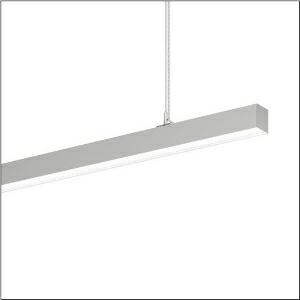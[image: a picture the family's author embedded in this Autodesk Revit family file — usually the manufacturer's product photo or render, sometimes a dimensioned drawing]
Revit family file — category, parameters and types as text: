
# Revit family: silica_r__21_51mx33tctds_657e
name_source: partatom
category: Lighting Fixtures
units: mm (PartAtom-declared; Revit-internal decimal feet)

## family parameters
Cut with Voids When Loaded = No
Host = Face
Light Source = No
Part Type = Normal
Room Calculation Point = No
Round Connector Dimension = Use Diameter
Shared = No

## types (1)
- --- (1 x LED, 14340 lm, 134.7 W, 6500K)
    Apparent Load = 135 VA
    CIE Flux Codes = 78 96 99 56 100
    Color Rendering = 80
    Color Temperature = 6500K
    Default Elevation = 1800 mm
    Description = Silica® 21, office luminaire, primary optical cover: prismatic diffuser, of PMMA, CAT 2 (L<= 3000cd/m²), light emission: direct/indirect distribution, primary light characteristic: symmetric, installation type: suspended mounting, LED, rated luminous flux: 14.340lm, luminous efficacy: 101lm/W, light colour: 8tw, colour temperature: 2700..6500K, control gear: DALI DT8, with terminal, 3+2-pole, max. 2.5mm², mains connection: 220..240V, AC, 50/60Hz, rated input power: 141.4W, luminaire housing, of aluminium, metallic grey (RAL 9006), length: 3.004mm, width: 53mm, height: 53mm, protection rating (complete): IP20, insulation class (complete): insulation class I (protective earthing), certification: CE, permissible operating ambient temperature: 0..+35°C, standard: EN 50419, packaging unit: 1 piece
    Height = 53 mm
    Lamp = 1 x LED
    Lamp Light Flux = 14340 lm
    Lamp Power = 134.7 W
    Lamp count = 1
    Length = 3004 mm
    Luminous efficacy = 106 lm/W
    Manufacturer = Siteco
    ModVariant = No
    Model = 51MX33TCTDS
    Mounting Place = Ceiling
    Mounting Type = Pendant
    Number of Poles = 1
    OnlyDefault = Yes
    Power Factor = 1
    Product Name = Silica® 21
    Product group = office luminaire | ceiling pendant
    ProductGroupID = 904
    Protection Class = Protection class I
    Protection Degree = IP 20
    RLX_Detail_Level = 1
    RLX_Emergency_Light_Flux = 0 lm
    RLX_Emergency_Type = 0
    RLX_Emergency_Type_DB = No
    RlxData = <blob elided: 20085 chars, md5=ac446b84>
    Socket = socket
    Standby Power = 0 W
    System Light Flux = 14340 lm
    System Power = 135 W
    Type Comments = individual setting
    Type Image = l_1335864.jpg
    URL = http://relux.com
    VarID = @adj_139734
    Voltage = 0 V
    Weight = 0.00 kg
    Width = 53 mm

## geometry (parser evidence)
native form markers: Blend x4, Sweep x14
no freeform markers — native parametric forms only
